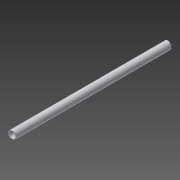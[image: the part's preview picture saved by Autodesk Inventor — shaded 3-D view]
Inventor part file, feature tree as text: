
AUTODESK INVENTOR PART (.ipt)
format: ipt  version: 2015 (Build 190159000, 159)  size: 108,032 bytes
history: native  units: mm
features: extrude x2, sketch x2, other x1, shell x1
ambient origin geometry x8: Origin, YZ Plane, XZ Plane, XY Plane, X Axis, Y Axis, Z Axis, Center Point
bodies: Body1 (feature_tree)
feature tree (6):
  other  "Bryła1"
  extrude  "Wyciągnięcie proste1"  Depth=20.0mm
  shell  "Skorupa1"  Thickness=400.0mm
  extrude  "Wyciągnięcie proste3"  Depth=2.0mm
  sketch  "Szkic1"
  sketch  "Szkic2"
